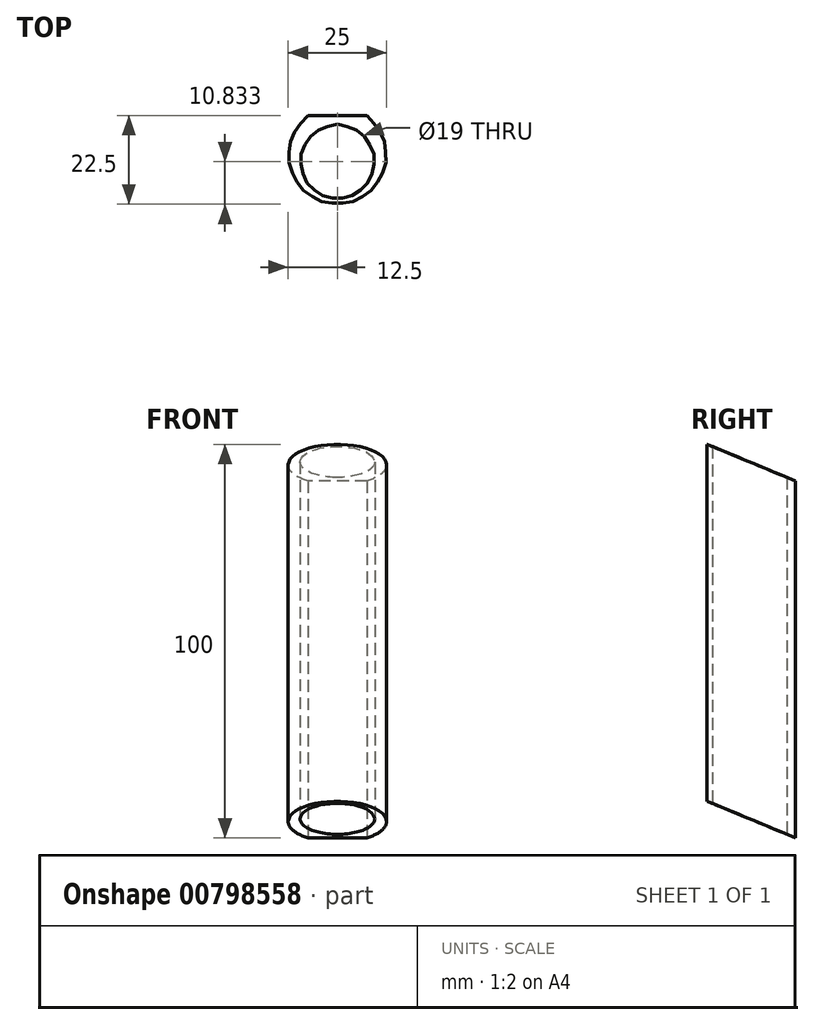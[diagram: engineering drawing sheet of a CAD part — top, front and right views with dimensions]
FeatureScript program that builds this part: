
annotation { "Feature Type Name" : "Feature", "Feature Type Description" : "" }
export const myFeature = defineFeature(function(context is Context, id is Id, definition is map)
    precondition{}
    {
        {
            var Q0;
            Q0=qCreatedBy(makeId("Top.planeOp"),FACE);
            var sketch = newSketch(context, id + "F0", { "sketchPlane" : qUnion([Q0])});
            skCircle(sketch, "E0", {"center": v(0, 0) * mm, "radius": 12.5 * mm});
            skLineSegment(sketch, "E1", {"start": v(-12.5, 0) * mm, "end": v(12.5, 0) * mm, "construction": true});
            skLineSegment(sketch, "E2", {"start": v(-7.5, 10) * mm, "end": v(7.5, 10) * mm});
            skLineSegment(sketch, "E3", {"start": v(-20.1, 9.81) * mm, "end": v(0, -25) * mm, "construction": true});
            skLineSegment(sketch, "E4", {"start": v(0, -25) * mm, "end": v(20.17, 9.94) * mm, "construction": true});
            skLineSegment(sketch, "E5", {"start": v(0, 12.5) * mm, "end": v(0, -12.5) * mm, "construction": true});
            skCircle(sketch, "E6", {"center": v(0, -1.67) * mm, "radius": 11.67 * mm, "construction": true});
            skCircle(sketch, "E7", {"center": v(0, -1.67) * mm, "radius": 9.5 * mm});
            skSolve(sketch);
        }
        {
            var Q0;
            {var subQ0=sQuery(id+"F0.wireOp",EDGE,"E2");Q0=makeQuery(id+"F0.imprint","IMPRINT",FACE,{"disambiguationData":[TD([[makeQuery(id+"F0.imprint","IMPRINT",EDGE,{"derivedFrom":subQ0}),-1.0]])]});}
            extrude(context, id + "F1", {"entities" : qUnion([Q0]), "depth" : 100 * mm, "offsetDistance" : 25 * mm});
        }
        {
            var Q0;
            Q0=qCreatedBy(makeId("Right.planeOp"),FACE);
            var sketch = newSketch(context, id + "F2", { "sketchPlane" : qUnion([Q0])});
            skLineSegment(sketch, "E8", {"start": v(-12.5, 0) * mm, "end": v(-12.5, 100) * mm});
            skLineSegment(sketch, "E9", {"start": v(-12.5, 100) * mm, "end": v(10, 90.68) * mm});
            skPoint(sketch, "E10.0", {"position": v(10, 0) * mm});
            skLineSegment(sketch, "E11", {"start": v(10, 0) * mm, "end": v(-12.5, 9.32) * mm});
            skPoint(sketch, "E12.0", {"position": v(10, 100) * mm});
            skPoint(sketch, "E13.0", {"position": v(-12.5, 0) * mm});
            skLineSegment(sketch, "E14", {"start": v(10, 90.68) * mm, "end": v(10, 100) * mm});
            skLineSegment(sketch, "E15", {"start": v(10, 100) * mm, "end": v(-12.5, 100) * mm});
            skLineSegment(sketch, "E16", {"start": v(10, 0) * mm, "end": v(-12.5, 0) * mm});
            skLineSegment(sketch, "E17", {"start": v(-12.5, 0) * mm, "end": v(-12.5, 9.32) * mm});
            skSolve(sketch);
        }
        {
            var Q0;
            Q0=makeQuery(id+"F2.imprint","IMPRINT",FACE,{"disambiguationData":[TD([[makeQuery(id+"F2.imprint","IMPRINT",EDGE,{"derivedFrom":sQuery(id+"F2.wireOp",EDGE,"E9")}),1.0]])]});
            var Q1;
            Q1=makeQuery(id+"F2.imprint","IMPRINT",FACE,{"disambiguationData":[TD([[makeQuery(id+"F2.imprint","IMPRINT",EDGE,{"derivedFrom":sQuery(id+"F2.wireOp",EDGE,"E11")}),1.0]])]});
            extrude(context, id + "F3", {"entities" : qUnion([Q0, Q1]), "depth" : 25 * mm, "offsetDistance" : 25 * mm, "hasSecondDirection" : true, "secondDirectionOppositeDirection" : true, "secondDirectionDepth" : 25 * mm});
        }
        {
            var Q0;
            Q0=makeQuery(id+"F3.opExtrude","SWEPT_BODY",BODY,{"disambiguationData":[OSD([sQuery(id+"F2.wireOp",EDGE,"E11"),sQuery(id+"F2.wireOp",EDGE,"E16"),sQuery(id+"F2.wireOp",EDGE,"E17")])]});
            var Q1;
            Q1=makeQuery(id+"F3.opExtrude","SWEPT_BODY",BODY,{"disambiguationData":[OSD([sQuery(id+"F2.wireOp",EDGE,"E9"),sQuery(id+"F2.wireOp",EDGE,"E14"),sQuery(id+"F2.wireOp",EDGE,"E15")])]});
            var Q2;
            Q2=makeQuery(id+"F1.opExtrude","SWEPT_BODY",BODY,{"disambiguationData":[OSD([sQuery(id+"F0.wireOp",EDGE,"E0"),sQuery(id+"F0.wireOp",EDGE,"E2"),sQuery(id+"F0.wireOp",EDGE,"E7")])]});
            booleanBodies(context, id + "F4", {"operationType" : BooleanOperationType.SUBTRACTION, "tools" : qUnion([Q0, Q1]), "targets" : qUnion([Q2])});
        }
    });
